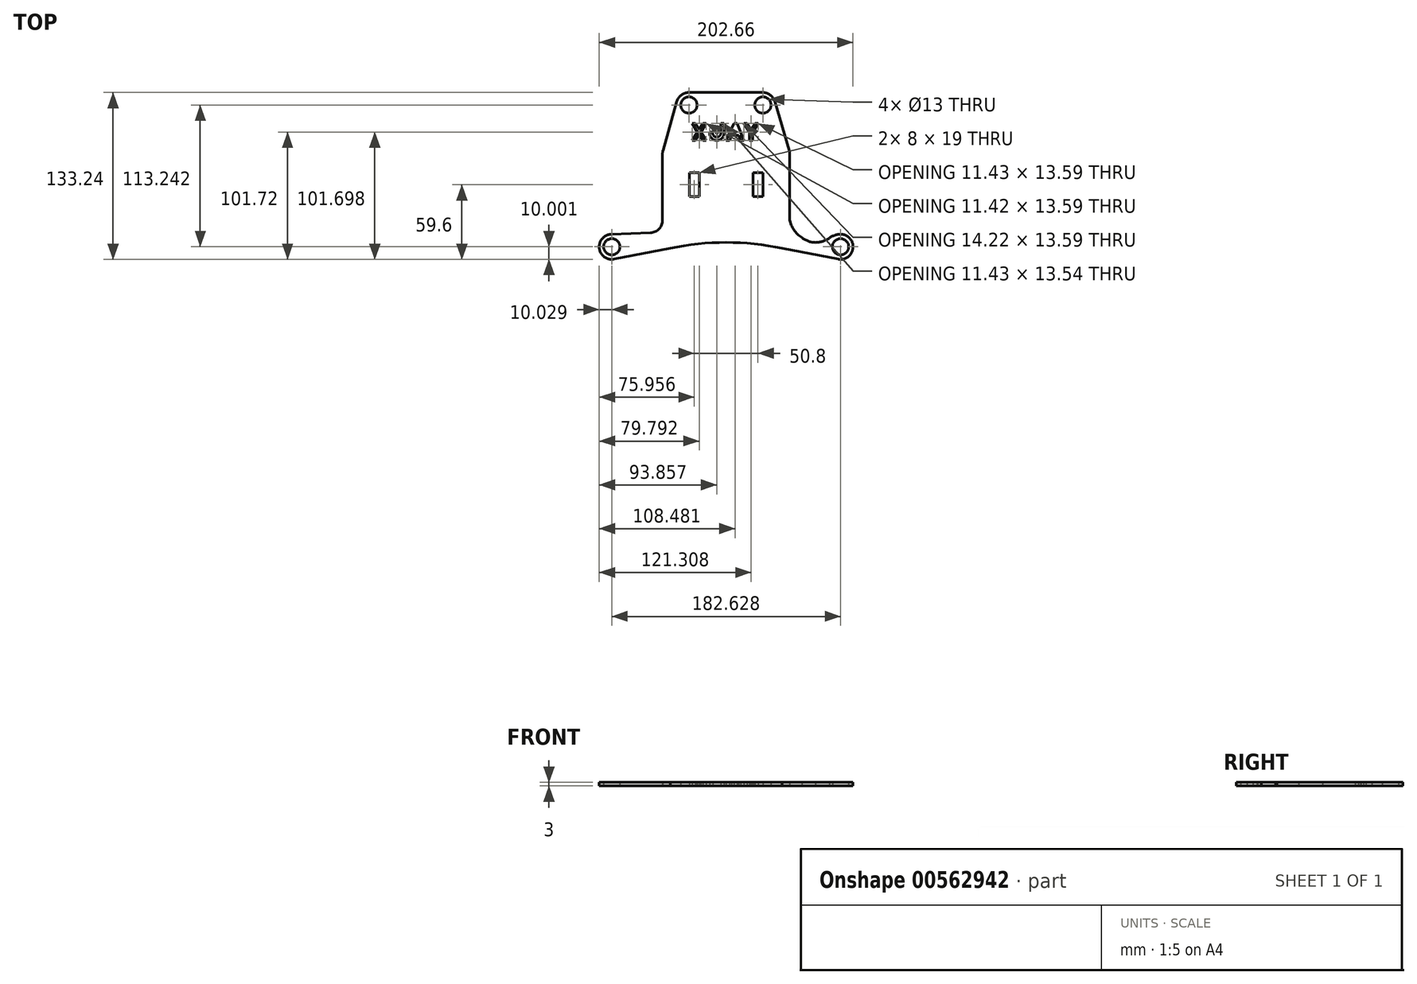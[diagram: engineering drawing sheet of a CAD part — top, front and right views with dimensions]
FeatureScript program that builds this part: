
annotation { "Feature Type Name" : "Feature", "Feature Type Description" : "" }
export const myFeature = defineFeature(function(context is Context, id is Id, definition is map)
    precondition{}
    {
        {
            var Q0;
            Q0=qCreatedBy(makeId("Top.planeOp"),FACE);
            var sketch = newSketch(context, id + "F0", { "sketchPlane" : qUnion([Q0])});
            skCircle(sketch, "E0", {"center": v(-29.75, 90.8) * mm, "radius": 6.5 * mm});
            skCircle(sketch, "E1", {"center": v(29.27, 90.8) * mm, "radius": 6.5 * mm});
            skCircle(sketch, "E2", {"center": v(-91.34, -22.45) * mm, "radius": 6.5 * mm});
            skCircle(sketch, "E3", {"center": v(91.29, -22.45) * mm, "radius": 6.5 * mm});
            skLineSegment(sketch, "E4.left", {"start": v(-50.83, 51.9) * mm, "end": v(-50.83, 0) * mm});
            skLineSegment(sketch, "E4.right", {"start": v(50.77, 51.85) * mm, "end": v(50.77, 0) * mm});
            skLineSegment(sketch, "E5", {"start": v(-50.44, 54.64) * mm, "end": v(-39.37, 93.53) * mm});
            skLineSegment(sketch, "E6", {"start": v(50.36, 54.69) * mm, "end": v(38.86, 93.63) * mm});
            skLineSegment(sketch, "E7", {"start": v(-29.75, 100.8) * mm, "end": v(29.27, 100.8) * mm});
            skArc(sketch, "E8", {"start": v(-91.72, -12.46) * mm, "mid": v(-101.3, -23.57) * mm, "end": v(-89.48, -32.27) * mm});
            skArc(sketch, "E9", {"start": v(89.4, -32.27) * mm, "mid": v(101.22, -23.58) * mm, "end": v(91.66, -12.46) * mm});
            skArc(sketch, "E10", {"start": v(-29.75, 100.8) * mm, "mid": v(-35.77, 98.77) * mm, "end": v(-39.37, 93.53) * mm});
            skArc(sketch, "E11", {"start": v(38.86, 93.63) * mm, "mid": v(35.26, 98.8) * mm, "end": v(29.27, 100.8) * mm});
            skPoint(sketch, "E12.visualSharp", {"position": v(-50.83, 53.3) * mm});
            skArc(sketch, "E12.filletArc", {"start": v(-50.44, 54.64) * mm, "mid": v(-50.73, 53.29) * mm, "end": v(-50.83, 51.9) * mm});
            skLineSegment(sketch, "E13", {"start": v(-50.83, 0) * mm, "end": v(-50.8, -0.9) * mm});
            skLineSegment(sketch, "E14", {"start": v(-91.72, -12.46) * mm, "end": v(-60.4, -11.28) * mm});
            skLineSegment(sketch, "E15", {"start": v(50.77, 0) * mm, "end": v(50.74, -0.9) * mm});
            skPoint(sketch, "E16.visualSharp", {"position": v(-50.42, -10.9) * mm});
            skArc(sketch, "E16.filletArc", {"start": v(-60.4, -11.28) * mm, "mid": v(-53.45, -8.08) * mm, "end": v(-50.8, -0.9) * mm});
            skPoint(sketch, "E17.visualSharp", {"position": v(50.36, -10.9) * mm});
            skPoint(sketch, "E18.visualSharp", {"position": v(50.77, 53.3) * mm});
            skArc(sketch, "E18.filletArc", {"start": v(50.77, 51.85) * mm, "mid": v(50.67, 53.29) * mm, "end": v(50.36, 54.69) * mm});
            skArc(sketch, "E19", {"start": v(44.7, -23.7) * mm, "mid": v(-0.03, -18.91) * mm, "end": v(-44.75, -23.7) * mm});
            skPoint(sketch, "E19.startSnap0", {"position": v(-44.75, -23.7) * mm});
            skLineSegment(sketch, "E20", {"start": v(-89.48, -32.27) * mm, "end": v(-44.75, -23.7) * mm});
            skLineSegment(sketch, "E21", {"start": v(89.4, -32.27) * mm, "end": v(44.7, -23.7) * mm});
            skArc(sketch, "E22", {"start": v(60.35, -15.13) * mm, "mid": v(65.53, -17.91) * mm, "end": v(71.3, -18.99) * mm});
            skArc(sketch, "E23", {"start": v(71.3, -18.99) * mm, "mid": v(77.03, -18.06) * mm, "end": v(82.26, -15.54) * mm});
            skArc(sketch, "E24", {"start": v(91.66, -12.46) * mm, "mid": v(86.68, -13.16) * mm, "end": v(82.26, -15.54) * mm});
            skArc(sketch, "E25", {"start": v(50.74, -0.9) * mm, "mid": v(54.18, -8.95) * mm, "end": v(60.35, -15.13) * mm});
            skLineSegment(sketch, "E26", {"start": v(-25.41, 26.65) * mm, "end": v(-21.41, 26.65) * mm});
            skLineSegment(sketch, "E27", {"start": v(-21.41, 26.65) * mm, "end": v(-29.41, 26.65) * mm});
            skLineSegment(sketch, "E28", {"start": v(-29.41, 26.65) * mm, "end": v(-29.41, 17.65) * mm});
            skLineSegment(sketch, "E29", {"start": v(-29.41, 17.65) * mm, "end": v(-21.41, 17.65) * mm});
            skLineSegment(sketch, "E30", {"start": v(-21.41, 17.65) * mm, "end": v(-21.41, 26.65) * mm});
            skLineSegment(sketch, "E31", {"start": v(-21.41, 26.65) * mm, "end": v(-21.41, 36.65) * mm});
            skLineSegment(sketch, "E32", {"start": v(-21.41, 36.65) * mm, "end": v(-29.41, 36.65) * mm});
            skLineSegment(sketch, "E33", {"start": v(-29.41, 36.65) * mm, "end": v(-29.41, 26.65) * mm});
            skLineSegment(sketch, "E34", {"start": v(25.39, 26.65) * mm, "end": v(21.39, 26.65) * mm});
            skLineSegment(sketch, "E35", {"start": v(21.39, 26.65) * mm, "end": v(29.39, 26.65) * mm});
            skLineSegment(sketch, "E36", {"start": v(29.39, 26.65) * mm, "end": v(29.39, 36.65) * mm});
            skLineSegment(sketch, "E37", {"start": v(29.39, 36.65) * mm, "end": v(21.39, 36.65) * mm});
            skLineSegment(sketch, "E38", {"start": v(21.39, 36.65) * mm, "end": v(21.39, 26.65) * mm});
            skLineSegment(sketch, "E39", {"start": v(21.39, 26.65) * mm, "end": v(21.39, 17.65) * mm});
            skLineSegment(sketch, "E40", {"start": v(21.39, 17.65) * mm, "end": v(29.39, 17.65) * mm});
            skLineSegment(sketch, "E41", {"start": v(29.39, 17.65) * mm, "end": v(29.39, 26.65) * mm});
            skLineSegment(sketch, "E42", {"start": v(-27.29, 76.04) * mm, "end": v(-18.43, 62.45) * mm});
            skLineSegment(sketch, "E43", {"start": v(-18.43, 62.45) * mm, "end": v(-15.87, 62.45) * mm});
            skLineSegment(sketch, "E44", {"start": v(-15.87, 62.45) * mm, "end": v(-24.72, 76.04) * mm});
            skLineSegment(sketch, "E45", {"start": v(-27.29, 62.45) * mm, "end": v(-18.43, 76.04) * mm});
            skLineSegment(sketch, "E46", {"start": v(-18.43, 76.04) * mm, "end": v(-15.87, 76.04) * mm});
            skLineSegment(sketch, "E47", {"start": v(-15.87, 76.04) * mm, "end": v(-24.72, 62.45) * mm});
            skLineSegment(sketch, "E48", {"start": v(-24.72, 62.45) * mm, "end": v(-27.29, 62.45) * mm});
            skArc(sketch, "E49", {"start": v(-13.23, 69.25) * mm, "mid": v(-7.51, 62.5) * mm, "end": v(-1.8, 69.25) * mm});
            skLineSegment(sketch, "E50", {"start": v(-1.8, 76.04) * mm, "end": v(-4.36, 76.04) * mm});
            skLineSegment(sketch, "E51", {"start": v(-4.36, 76.04) * mm, "end": v(-4.36, 69.25) * mm});
            skLineSegment(sketch, "E52", {"start": v(-13.23, 69.25) * mm, "end": v(-10.66, 69.25) * mm});
            skArc(sketch, "E53", {"start": v(-10.66, 69.25) * mm, "mid": v(-7.51, 65.14) * mm, "end": v(-4.36, 69.25) * mm});
            skLineSegment(sketch, "E54", {"start": v(-1.8, 69.25) * mm, "end": v(-1.8, 76.04) * mm});
            skLineSegment(sketch, "E55", {"start": v(0, 62.45) * mm, "end": v(6.07, 76.04) * mm});
            skLineSegment(sketch, "E56", {"start": v(6.07, 76.04) * mm, "end": v(8.63, 76.04) * mm});
            skLineSegment(sketch, "E57", {"start": v(8.63, 76.04) * mm, "end": v(14.22, 62.45) * mm});
            skLineSegment(sketch, "E58", {"start": v(14.22, 62.45) * mm, "end": v(11.66, 62.45) * mm});
            skLineSegment(sketch, "E59", {"start": v(11.66, 62.45) * mm, "end": v(6.07, 76.04) * mm});
            skLineSegment(sketch, "E60", {"start": v(8.63, 76.04) * mm, "end": v(2.57, 62.45) * mm});
            skLineSegment(sketch, "E61", {"start": v(2.57, 62.45) * mm, "end": v(0, 62.45) * mm});
            skLineSegment(sketch, "E62", {"start": v(3.03, 69.25) * mm, "end": v(11.43, 69.25) * mm});
            skLineSegment(sketch, "E63", {"start": v(3.03, 69.25) * mm, "end": v(3.03, 66.68) * mm});
            skLineSegment(sketch, "E64", {"start": v(3.03, 66.68) * mm, "end": v(12.48, 66.68) * mm});
            skLineSegment(sketch, "E65", {"start": v(14.22, 76.04) * mm, "end": v(16.79, 76.04) * mm});
            skLineSegment(sketch, "E66", {"start": v(23.09, 76.04) * mm, "end": v(25.65, 76.04) * mm});
            skLineSegment(sketch, "E67", {"start": v(19.94, 62.45) * mm, "end": v(21.2, 62.45) * mm});
            skLineSegment(sketch, "E68", {"start": v(21.2, 62.45) * mm, "end": v(18.67, 62.45) * mm});
            skLineSegment(sketch, "E69", {"start": v(18.67, 62.45) * mm, "end": v(18.67, 69.23) * mm});
            skLineSegment(sketch, "E70", {"start": v(21.2, 62.45) * mm, "end": v(21.2, 69.23) * mm});
            skLineSegment(sketch, "E71", {"start": v(14.22, 76.04) * mm, "end": v(18.67, 69.23) * mm});
            skLineSegment(sketch, "E72", {"start": v(21.2, 69.23) * mm, "end": v(25.65, 76.04) * mm});
            skLineSegment(sketch, "E73", {"start": v(16.79, 76.04) * mm, "end": v(19.94, 71.21) * mm});
            skPoint(sketch, "E73.endSnap0", {"position": v(19.94, 76.04) * mm});
            skLineSegment(sketch, "E74", {"start": v(19.94, 71.21) * mm, "end": v(23.09, 76.04) * mm});
            skLineSegment(sketch, "E75", {"start": v(-27.29, 76.04) * mm, "end": v(-24.72, 76.04) * mm});
            skSolve(sketch);
        }
        {
            var Q0;
            Q0=makeQuery(id+"F0.imprint","IMPRINT",FACE,{"disambiguationData":[TD([[makeQuery(id+"F0.imprint","IMPRINT",EDGE,{"derivedFrom":sQuery(id+"F0.wireOp",EDGE,"E0")}),-1.0]])]});
            extrude(context, id + "F1", {"entities" : qUnion([Q0]), "depth" : 3 * mm, "offsetDistance" : 25.4 * mm});
        }
    });
